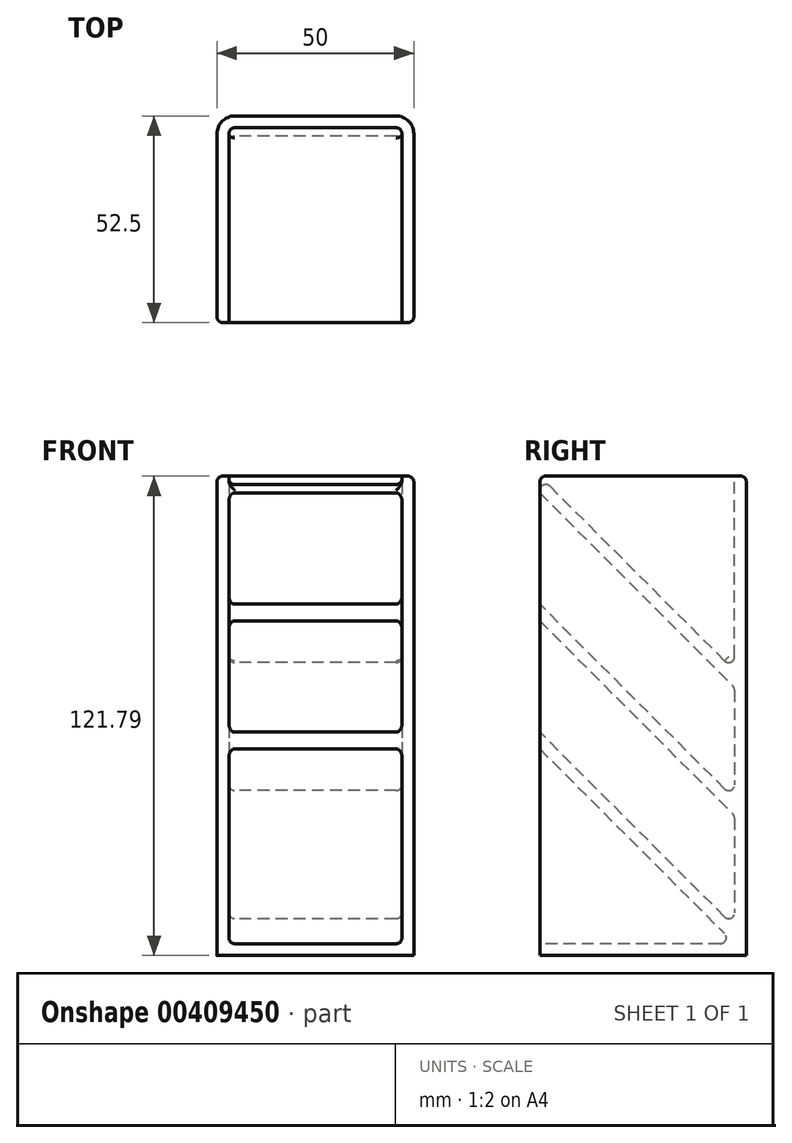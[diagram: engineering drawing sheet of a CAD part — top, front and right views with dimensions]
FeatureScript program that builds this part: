
annotation { "Feature Type Name" : "Feature", "Feature Type Description" : "" }
export const myFeature = defineFeature(function(context is Context, id is Id, definition is map)
    precondition{}
    {
        {
            var Q0;
            Q0=qCreatedBy(makeId("Right.planeOp"),FACE);
            var sketch = newSketch(context, id + "F0", { "sketchPlane" : qUnion([Q0])});
            skLineSegment(sketch, "E0", {"start": v(-3, 3) * mm, "end": v(-52.5, 3) * mm});
            skLineSegment(sketch, "E1", {"start": v(-52.5, 3) * mm, "end": v(-52.5, 52.5) * mm});
            skLineSegment(sketch, "E2", {"start": v(-52.5, 52.5) * mm, "end": v(-3, 3) * mm});
            skLineSegment(sketch, "E3", {"start": v(-3, 7.24) * mm, "end": v(-52.5, 56.74) * mm});
            skLineSegment(sketch, "E4", {"start": v(-52.5, 56.74) * mm, "end": v(-52.5, 85.02) * mm});
            skLineSegment(sketch, "E5", {"start": v(-52.5, 85.02) * mm, "end": v(-3, 35.53) * mm});
            skLineSegment(sketch, "E6", {"start": v(-3, 35.53) * mm, "end": v(-3, 7.24) * mm});
            skLineSegment(sketch, "E7", {"start": v(-3, 39.77) * mm, "end": v(-52.5, 89.27) * mm});
            skLineSegment(sketch, "E8", {"start": v(-52.5, 89.27) * mm, "end": v(-52.5, 117.55) * mm});
            skLineSegment(sketch, "E9", {"start": v(-52.5, 117.55) * mm, "end": v(-3, 68.05) * mm});
            skLineSegment(sketch, "E10", {"start": v(-3, 68.05) * mm, "end": v(-3, 39.77) * mm});
            skLineSegment(sketch, "E11", {"start": v(-52.5, 121.8) * mm, "end": v(-3, 72.3) * mm});
            skLineSegment(sketch, "E12", {"start": v(-3, 72.3) * mm, "end": v(-3, 121.8) * mm});
            skLineSegment(sketch, "E13", {"start": v(-3, 121.8) * mm, "end": v(-52.5, 121.8) * mm});
            skSolve(sketch);
        }
        {
            var Q0;
            Q0=qCreatedBy(makeId("Right.planeOp"),FACE);
            var sketch = newSketch(context, id + "F1", { "sketchPlane" : qUnion([Q0])});
            skLineSegment(sketch, "E14.bottom", {"start": v(0, 0) * mm, "end": v(-52.5, 0) * mm});
            skLineSegment(sketch, "E14.top", {"start": v(0, 121.8) * mm, "end": v(-52.5, 121.8) * mm});
            skLineSegment(sketch, "E14.left", {"start": v(0, 0) * mm, "end": v(0, 121.8) * mm});
            skLineSegment(sketch, "E14.right", {"start": v(-52.5, 0) * mm, "end": v(-52.5, 121.8) * mm});
            skSolve(sketch);
        }
        {
            var Q0;
            Q0 = qSketchRegion(id + "F1", true);
            extrude(context, id + "F2", {"entities" : qUnion([Q0]), "endBound" : BoundingType.SYMMETRIC, "depth" : 50 * mm});
        }
        {
            var Q0;
            Q0 = qSketchRegion(id + "F0", true);
            extrude(context, id + "F3", {"entities" : qUnion([Q0]), "operationType" : NewBodyOperationType.REMOVE, "endBound" : BoundingType.SYMMETRIC, "oppositeDirection" : true, "depth" : 44 * mm});
        }
        {
            var Q0;
            Q0=makeQuery(id+"F0.imprint","IMPRINT",FACE,{"disambiguationData":[TD([[makeQuery(id+"F0.imprint","IMPRINT",EDGE,{"derivedFrom":sQuery(id+"F0.wireOp",EDGE,"E11")}),1.0]])]});
            var sketch = newSketch(context, id + "F4", { "sketchPlane" : qUnion([Q0])});
            skLineSegment(sketch, "E15", {"start": v(-52.5, 121.8) * mm, "end": v(-52.5, 118.17) * mm});
            skPoint(sketch, "E16.start.orphan", {"position": v(-51.16, 120.46) * mm});
            skArc(sketch, "E17", {"start": v(-52.5, 118.17) * mm, "mid": v(-51.57, 119.56) * mm, "end": v(-49.94, 119.23) * mm});
            skLineSegment(sketch, "E18", {"start": v(-52.5, 121.8) * mm, "end": v(-49.94, 119.23) * mm});
            skSolve(sketch);
        }
        {
            var Q0;
            Q0 = qSketchRegion(id + "F4", true);
            extrude(context, id + "F5", {"entities" : qUnion([Q0]), "operationType" : NewBodyOperationType.REMOVE, "endBound" : BoundingType.SYMMETRIC, "oppositeDirection" : true, "depth" : 44 * mm, "hasSecondDirection" : true, "secondDirectionOppositeDirection" : false, "secondDirectionDepth" : 22 * mm});
        }
        {
            var Q0;
            Q0=makeQuery(id+"F2.opExtrude","CAP_EDGE",EDGE,{"disambiguationData":[OSD([sQuery(id+"F1.wireOp",EDGE,"E14.top")])],"isStart":false});
            var Q1;
            Q1=makeQuery(id+"F2.opExtrude","SWEPT_EDGE",EDGE,{"disambiguationData":[OSD([sQuery(id+"F1.wireOp",EDGE,"E14.top"),sQuery(id+"F1.wireOp",EDGE,"E14.left")])]});
            var Q2;
            Q2=makeQuery(id+"F2.opExtrude","CAP_EDGE",EDGE,{"disambiguationData":[OSD([sQuery(id+"F1.wireOp",EDGE,"E14.top")])],"isStart":true});
            var Q3;
            Q3=makeQuery(id+"F3.boolean.opBoolean","COPY",EDGE,{"derivedFrom":makeQuery(id+"F3.opExtrude","CAP_EDGE",EDGE,{"disambiguationData":[OSD([sQuery(id+"F0.wireOp",EDGE,"E13")])],"isStart":false})});
            var Q4;
            Q4=makeQuery(id+"F3.boolean.opBoolean","COPY",EDGE,{"derivedFrom":makeQuery(id+"F3.opExtrude","SWEPT_EDGE",EDGE,{"disambiguationData":[OSD([sQuery(id+"F0.wireOp",EDGE,"E12"),sQuery(id+"F0.wireOp",EDGE,"E13")])]})});
            var Q5;
            Q5=makeQuery(id+"F3.boolean.opBoolean","COPY",EDGE,{"derivedFrom":makeQuery(id+"F3.opExtrude","CAP_EDGE",EDGE,{"disambiguationData":[OSD([sQuery(id+"F0.wireOp",EDGE,"E13")])],"isStart":true})});
            var Q6;
            Q6=makeQuery(id+"F3.boolean.opBoolean","COPY",EDGE,{"derivedFrom":makeQuery(id+"F3.opExtrude","CAP_EDGE",EDGE,{"disambiguationData":[OSD([sQuery(id+"F0.wireOp",EDGE,"E12")])],"isStart":false})});
            var Q7;
            Q7=makeQuery(id+"F3.boolean.opBoolean","COPY",EDGE,{"derivedFrom":makeQuery(id+"F3.opExtrude","CAP_EDGE",EDGE,{"disambiguationData":[OSD([sQuery(id+"F0.wireOp",EDGE,"E12")])],"isStart":true})});
            var Q8;
            Q8=makeQuery(id+"F2.opExtrude","CAP_EDGE",EDGE,{"disambiguationData":[OSD([sQuery(id+"F1.wireOp",EDGE,"E14.right")])],"isStart":false});
            var Q9;
            Q9=makeQuery(id+"F3.boolean.opBoolean","COPY",EDGE,{"derivedFrom":makeQuery(id+"F3.opExtrude","CAP_EDGE",EDGE,{"disambiguationData":[OSD([sQuery(id+"F0.wireOp",EDGE,"E1")])],"isStart":true})});
            var Q10;
            Q10=makeQuery(id+"F3.boolean.opBoolean","COPY",EDGE,{"derivedFrom":makeQuery(id+"F3.opExtrude","CAP_EDGE",EDGE,{"disambiguationData":[OSD([sQuery(id+"F0.wireOp",EDGE,"E4")])],"isStart":true})});
            var Q11;
            Q11=makeQuery(id+"F3.boolean.opBoolean","COPY",EDGE,{"derivedFrom":makeQuery(id+"F3.opExtrude","CAP_EDGE",EDGE,{"disambiguationData":[OSD([sQuery(id+"F0.wireOp",EDGE,"E8")])],"isStart":true})});
            var Q12;
            Q12=makeQuery(id+"F3.boolean.opBoolean","COPY",EDGE,{"derivedFrom":makeQuery(id+"F3.opExtrude","CAP_EDGE",EDGE,{"disambiguationData":[OSD([sQuery(id+"F0.wireOp",EDGE,"E8")])],"isStart":false})});
            var Q13;
            Q13=makeQuery(id+"F3.boolean.opBoolean","COPY",EDGE,{"derivedFrom":makeQuery(id+"F3.opExtrude","CAP_EDGE",EDGE,{"disambiguationData":[OSD([sQuery(id+"F0.wireOp",EDGE,"E4")])],"isStart":false})});
            var Q14;
            Q14=makeQuery(id+"F3.boolean.opBoolean","COPY",EDGE,{"derivedFrom":makeQuery(id+"F3.opExtrude","CAP_EDGE",EDGE,{"disambiguationData":[OSD([sQuery(id+"F0.wireOp",EDGE,"E1")])],"isStart":false})});
            var Q15;
            Q15=makeQuery(id+"F2.opExtrude","CAP_EDGE",EDGE,{"disambiguationData":[OSD([sQuery(id+"F1.wireOp",EDGE,"E14.right")])],"isStart":true});
            var Q16;
            Q16=makeQuery(id+"F3.boolean.opBoolean","COPY",EDGE,{"derivedFrom":makeQuery(id+"F3.opExtrude","CAP_EDGE",EDGE,{"disambiguationData":[OSD([sQuery(id+"F0.wireOp",EDGE,"E10")])],"isStart":false})});
            var Q17;
            Q17=makeQuery(id+"F3.boolean.opBoolean","COPY",EDGE,{"derivedFrom":makeQuery(id+"F3.opExtrude","CAP_EDGE",EDGE,{"disambiguationData":[OSD([sQuery(id+"F0.wireOp",EDGE,"E10")])],"isStart":true})});
            var Q18;
            Q18=makeQuery(id+"F3.boolean.opBoolean","COPY",EDGE,{"derivedFrom":makeQuery(id+"F3.opExtrude","CAP_EDGE",EDGE,{"disambiguationData":[OSD([sQuery(id+"F0.wireOp",EDGE,"E6")])],"isStart":true})});
            var Q19;
            Q19=makeQuery(id+"F3.boolean.opBoolean","COPY",EDGE,{"derivedFrom":makeQuery(id+"F3.opExtrude","CAP_EDGE",EDGE,{"disambiguationData":[OSD([sQuery(id+"F0.wireOp",EDGE,"E6")])],"isStart":false})});
            var Q20;
            Q20=makeQuery(id+"F3.boolean.opBoolean","COPY",EDGE,{"derivedFrom":makeQuery(id+"F3.opExtrude","CAP_EDGE",EDGE,{"disambiguationData":[OSD([sQuery(id+"F0.wireOp",EDGE,"E0")])],"isStart":false})});
            var Q21;
            Q21=makeQuery(id+"F3.boolean.opBoolean","COPY",EDGE,{"derivedFrom":makeQuery(id+"F3.opExtrude","CAP_EDGE",EDGE,{"disambiguationData":[OSD([sQuery(id+"F0.wireOp",EDGE,"E0")])],"isStart":true})});
            var Q22;
            Q22=makeQuery(id+"F3.boolean.opBoolean","COPY",EDGE,{"derivedFrom":makeQuery(id+"F3.opExtrude","CAP_EDGE",EDGE,{"disambiguationData":[OSD([sQuery(id+"F0.wireOp",EDGE,"E2")])],"isStart":true})});
            var Q23;
            Q23=makeQuery(id+"F3.boolean.opBoolean","COPY",EDGE,{"derivedFrom":makeQuery(id+"F3.opExtrude","CAP_EDGE",EDGE,{"disambiguationData":[OSD([sQuery(id+"F0.wireOp",EDGE,"E2")])],"isStart":false})});
            var Q24;
            Q24=makeQuery(id+"F3.boolean.opBoolean","COPY",EDGE,{"derivedFrom":makeQuery(id+"F3.opExtrude","CAP_EDGE",EDGE,{"disambiguationData":[OSD([sQuery(id+"F0.wireOp",EDGE,"E3")])],"isStart":false})});
            var Q25;
            Q25=makeQuery(id+"F3.boolean.opBoolean","COPY",EDGE,{"derivedFrom":makeQuery(id+"F3.opExtrude","CAP_EDGE",EDGE,{"disambiguationData":[OSD([sQuery(id+"F0.wireOp",EDGE,"E5")])],"isStart":false})});
            var Q26;
            Q26=makeQuery(id+"F3.boolean.opBoolean","COPY",EDGE,{"derivedFrom":makeQuery(id+"F3.opExtrude","CAP_EDGE",EDGE,{"disambiguationData":[OSD([sQuery(id+"F0.wireOp",EDGE,"E5")])],"isStart":true})});
            var Q27;
            Q27=makeQuery(id+"F3.boolean.opBoolean","COPY",EDGE,{"derivedFrom":makeQuery(id+"F3.opExtrude","CAP_EDGE",EDGE,{"disambiguationData":[OSD([sQuery(id+"F0.wireOp",EDGE,"E3")])],"isStart":true})});
            var Q28;
            Q28=makeQuery(id+"F3.boolean.opBoolean","COPY",EDGE,{"derivedFrom":makeQuery(id+"F3.opExtrude","CAP_EDGE",EDGE,{"disambiguationData":[OSD([sQuery(id+"F0.wireOp",EDGE,"E7")])],"isStart":true})});
            var Q29;
            Q29=makeQuery(id+"F3.boolean.opBoolean","COPY",EDGE,{"derivedFrom":makeQuery(id+"F3.opExtrude","CAP_EDGE",EDGE,{"disambiguationData":[OSD([sQuery(id+"F0.wireOp",EDGE,"E9")])],"isStart":true})});
            var Q30;
            Q30=makeQuery(id+"F3.boolean.opBoolean","COPY",EDGE,{"derivedFrom":makeQuery(id+"F3.opExtrude","CAP_EDGE",EDGE,{"disambiguationData":[OSD([sQuery(id+"F0.wireOp",EDGE,"E7")])],"isStart":false})});
            var Q31;
            Q31=makeQuery(id+"F3.boolean.opBoolean","COPY",EDGE,{"derivedFrom":makeQuery(id+"F3.opExtrude","CAP_EDGE",EDGE,{"disambiguationData":[OSD([sQuery(id+"F0.wireOp",EDGE,"E9")])],"isStart":false})});
            var Q32;
            Q32=makeQuery(id+"F3.boolean.opBoolean","COPY",EDGE,{"derivedFrom":makeQuery(id+"F3.opExtrude","SWEPT_EDGE",EDGE,{"disambiguationData":[OSD([sQuery(id+"F0.wireOp",EDGE,"E0"),sQuery(id+"F0.wireOp",EDGE,"E2")])]})});
            var Q33;
            Q33=makeQuery(id+"F3.boolean.opBoolean","COPY",EDGE,{"derivedFrom":makeQuery(id+"F3.opExtrude","SWEPT_EDGE",EDGE,{"disambiguationData":[OSD([sQuery(id+"F0.wireOp",EDGE,"E3"),sQuery(id+"F0.wireOp",EDGE,"E6")])]})});
            var Q34;
            Q34=makeQuery(id+"F3.boolean.opBoolean","COPY",EDGE,{"derivedFrom":makeQuery(id+"F3.opExtrude","SWEPT_EDGE",EDGE,{"disambiguationData":[OSD([sQuery(id+"F0.wireOp",EDGE,"E5"),sQuery(id+"F0.wireOp",EDGE,"E6")])]})});
            var Q35;
            Q35=makeQuery(id+"F3.boolean.opBoolean","COPY",EDGE,{"derivedFrom":makeQuery(id+"F3.opExtrude","SWEPT_EDGE",EDGE,{"disambiguationData":[OSD([sQuery(id+"F0.wireOp",EDGE,"E7"),sQuery(id+"F0.wireOp",EDGE,"E10")])]})});
            var Q36;
            Q36=makeQuery(id+"F3.boolean.opBoolean","COPY",EDGE,{"derivedFrom":makeQuery(id+"F3.opExtrude","SWEPT_EDGE",EDGE,{"disambiguationData":[OSD([sQuery(id+"F0.wireOp",EDGE,"E9"),sQuery(id+"F0.wireOp",EDGE,"E10")])]})});
            var Q37;
            Q37=makeQuery(id+"F3.boolean.opBoolean","COPY",EDGE,{"derivedFrom":makeQuery(id+"F3.opExtrude","SWEPT_EDGE",EDGE,{"disambiguationData":[OSD([sQuery(id+"F0.wireOp",EDGE,"E11"),sQuery(id+"F0.wireOp",EDGE,"E12")])]})});
            fillet(context, id + "F6", {"entities" : qUnion([Q0, Q1, Q2, Q3, Q4, Q5, Q6, Q7, Q8, Q9, Q10, Q11, Q12, Q13, Q14, Q15, Q16, Q17, Q18, Q19, Q20, Q21, Q22, Q23, Q24, Q25, Q26, Q27, Q28, Q29, Q30, Q31, Q32, Q33, Q34, Q35, Q36, Q37]), "radius" : 1.5 * mm, "tangentPropagation" : true, "allowEdgeOverflow" : false});
        }
        {
            var Q0;
            Q0=makeQuery(id+"F6.opFillet","BLEND_EDGE",EDGE,{"blendedFrom":[makeQuery(id+"F2.opExtrude","CAP_EDGE",EDGE,{"disambiguationData":[OSD([sQuery(id+"F1.wireOp",EDGE,"E14.top")])],"isStart":true}),makeQuery(id+"F2.opExtrude","CAP_EDGE",EDGE,{"disambiguationData":[OSD([sQuery(id+"F1.wireOp",EDGE,"E14.right")])],"isStart":true})],"blendedInto":[]});
            var Q1;
            Q1=makeQuery(id+"F6.opFillet","BLEND_EDGE",EDGE,{"blendedFrom":[makeQuery(id+"F2.opExtrude","CAP_EDGE",EDGE,{"disambiguationData":[OSD([sQuery(id+"F1.wireOp",EDGE,"E14.top")])],"isStart":false}),makeQuery(id+"F2.opExtrude","CAP_EDGE",EDGE,{"disambiguationData":[OSD([sQuery(id+"F1.wireOp",EDGE,"E14.right")])],"isStart":false})],"blendedInto":[]});
            fillet(context, id + "F7", {"entities" : qUnion([Q0, Q1]), "radius" : 1.5 * mm, "tangentPropagation" : true, "allowEdgeOverflow" : false});
        }
        {
            var Q0;
            Q0=makeQuery(id+"F3.boolean.opBoolean","COPY",EDGE,{"derivedFrom":makeQuery(id+"F3.opExtrude","CAP_EDGE",EDGE,{"disambiguationData":[OSD([sQuery(id+"F0.wireOp",EDGE,"E11")])],"isStart":false})});
            var Q1;
            Q1=makeQuery(id+"F3.boolean.opBoolean","COPY",EDGE,{"derivedFrom":makeQuery(id+"F3.opExtrude","CAP_EDGE",EDGE,{"disambiguationData":[OSD([sQuery(id+"F0.wireOp",EDGE,"E11")])],"isStart":true})});
            fillet(context, id + "F8", {"entities" : qUnion([Q0, Q1]), "radius" : 1.5 * mm, "tangentPropagation" : true, "allowEdgeOverflow" : false});
        }
        {
            var Q0;
            Q0=makeQuery(id+"F2.opExtrude","CAP_EDGE",EDGE,{"disambiguationData":[OSD([sQuery(id+"F1.wireOp",EDGE,"E14.left")])],"isStart":false});
            var Q1;
            Q1=makeQuery(id+"F2.opExtrude","CAP_EDGE",EDGE,{"disambiguationData":[OSD([sQuery(id+"F1.wireOp",EDGE,"E14.left")])],"isStart":true});
            fillet(context, id + "F9", {"entities" : qUnion([Q0, Q1]), "radius" : 4.5 * mm, "tangentPropagation" : true, "allowEdgeOverflow" : false});
        }
    });
